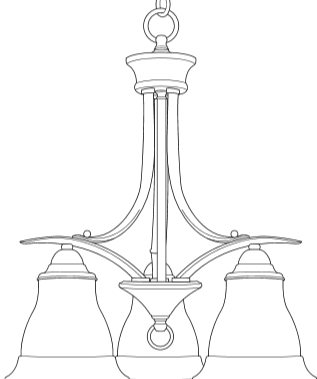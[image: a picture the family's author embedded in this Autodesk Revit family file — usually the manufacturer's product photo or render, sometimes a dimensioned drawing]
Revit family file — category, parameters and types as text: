
# Revit family: P4417-77 9-100W MED CHANDELEIR 6 AND 3
name_source: partatom
category: Lighting Fixtures
revit_build: Autodesk Revit Architecture 2012 (Build: 20110309_2315(x64)
units: mm (PartAtom-declared; Revit-internal decimal feet)

## types (1)
- P4417-77 9-100W MED CHANDELEIR 6 AND 3
    Ceiling Chain = Forged Bronze
    Celing chain length = 40"
    Chandelier = Forged Bronze
    Default Elevation = 48"
    Description = Six-light, two-tier chandelier with three-light downlight in tea stained oversized, bell-shaped glass bowl. Distinctive ebbing and flowing of squared scrolls and arms in Forged Bronze finish.
    Family = Trinity
    Glass = Tea Stained Glass
    Lamp = Six
    Manufacturer = Progress Lighting
    Manufacturer Fax = 864-678-1065
    Model = P4417-77
    Mounting = Chain Hung Ceiling Mount
    Product Documentation Link = http://progresslighting.com
    Product Page URL = http://progresslighting.com
    URL = http://progresslighting.com
    Wattage Comments = 100 W

## geometry (parser evidence)
native form markers: Sweep x12
no freeform markers — native parametric forms only
